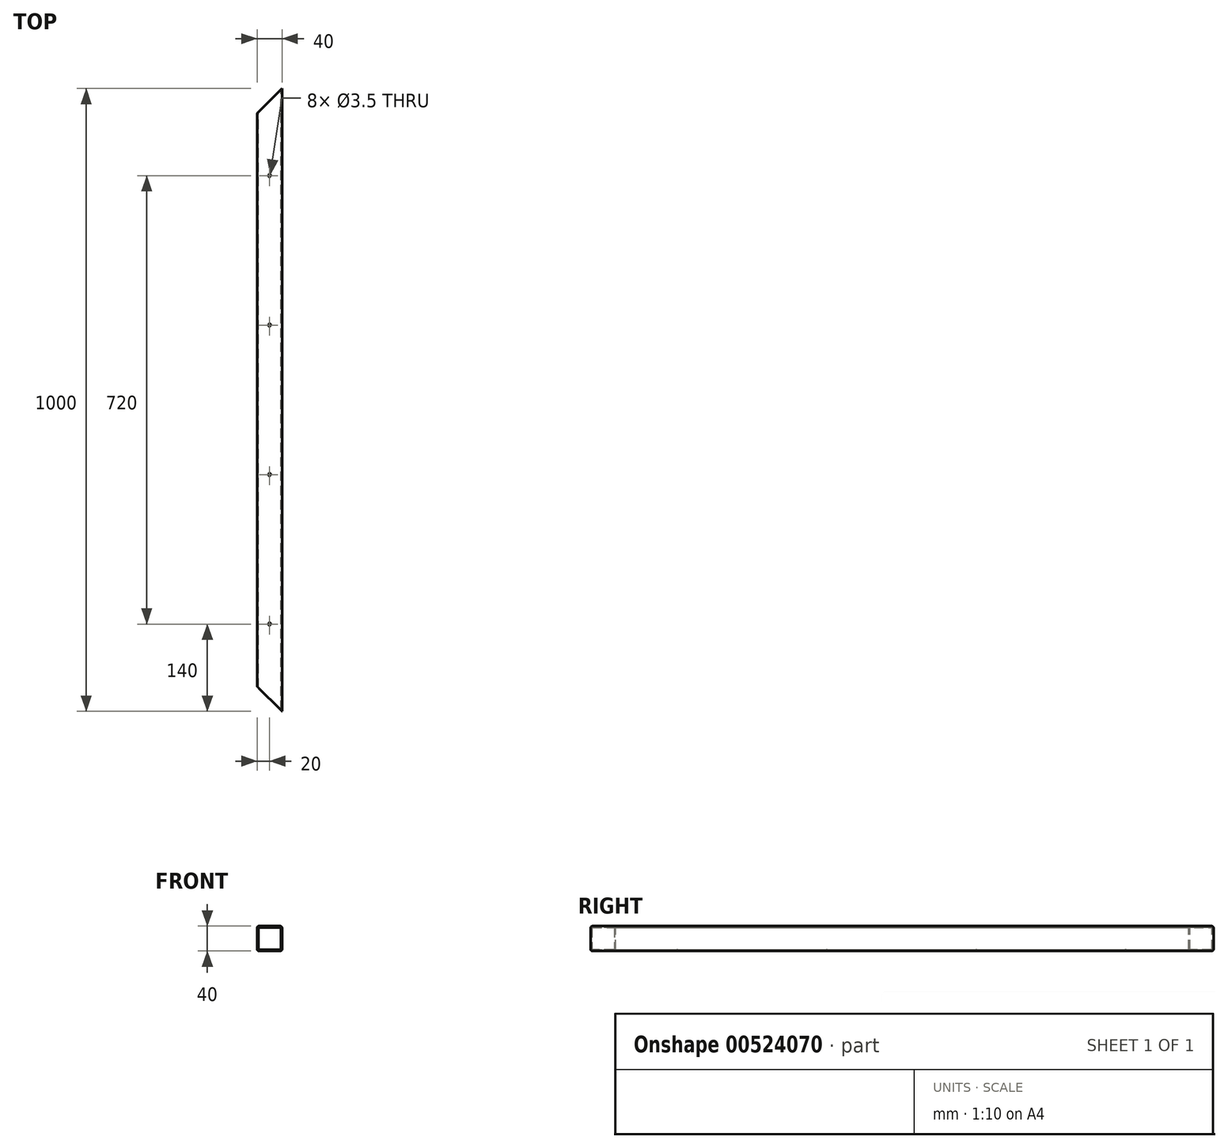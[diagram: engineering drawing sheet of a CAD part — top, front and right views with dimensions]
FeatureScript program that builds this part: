
annotation { "Feature Type Name" : "Feature", "Feature Type Description" : "" }
export const myFeature = defineFeature(function(context is Context, id is Id, definition is map)
    precondition{}
    {
        {
            assignVariable(context, id + "F0", {"name" : "R", "anyValue" : 3});
        }
        {
            assignVariable(context, id + "F1", {"name" : "W", "anyValue" : 2});
        }
        {
            var Q0;
            Q0=qCreatedBy(makeId("Front.planeOp"),FACE);
            var sketch = newSketch(context, id + "F2", { "sketchPlane" : qUnion([Q0])});
            skLineSegment(sketch, "E0.bottom", {"start": v(-20, 20) * mm, "end": v(20, 20) * mm});
            skLineSegment(sketch, "E0.top", {"start": v(-20, -20) * mm, "end": v(20, -20) * mm});
            skLineSegment(sketch, "E0.left", {"start": v(-20, 20) * mm, "end": v(-20, -20) * mm});
            skLineSegment(sketch, "E0.right", {"start": v(20, 20) * mm, "end": v(20, -20) * mm});
            skSolve(sketch);
        }
        {
            var Q0;
            Q0=qSketchRegion(id+"F2",true);
            extrude(context, id + "F3", {"entities" : qUnion([Q0]), "endBound" : BoundingType.SYMMETRIC, "depth" : 1000 * mm, "offsetDistance" : 25 * mm});
        }
        {
            var Q0;
            Q0=makeQuery(id+"F3.opExtrude","SWEPT_EDGE",EDGE,{"disambiguationData":[OSD([sQuery(id+"F2.wireOp",EDGE,"E0.bottom"),sQuery(id+"F2.wireOp",EDGE,"E0.right")])]});
            var Q1;
            Q1=makeQuery(id+"F3.opExtrude","SWEPT_EDGE",EDGE,{"disambiguationData":[OSD([sQuery(id+"F2.wireOp",EDGE,"E0.bottom"),sQuery(id+"F2.wireOp",EDGE,"E0.left")])]});
            var Q2;
            Q2=makeQuery(id+"F3.opExtrude","SWEPT_EDGE",EDGE,{"disambiguationData":[OSD([sQuery(id+"F2.wireOp",EDGE,"E0.top"),sQuery(id+"F2.wireOp",EDGE,"E0.right")])]});
            var Q3;
            Q3=makeQuery(id+"F3.opExtrude","SWEPT_EDGE",EDGE,{"disambiguationData":[OSD([sQuery(id+"F2.wireOp",EDGE,"E0.top"),sQuery(id+"F2.wireOp",EDGE,"E0.left")])]});
            fillet(context, id + "F4", {"entities" : qUnion([Q0, Q1, Q2, Q3]), "radius" : (getVariable(context, 'R')) * mm, "tangentPropagation" : true, "allowEdgeOverflow" : false});
        }
        {
            var Q0;
            Q0=makeQuery(id+"F3.opExtrude","CAP_FACE",FACE,{"disambiguationData":[OSD([sQuery(id+"F2.wireOp",EDGE,"E0.bottom"),sQuery(id+"F2.wireOp",EDGE,"E0.top"),sQuery(id+"F2.wireOp",EDGE,"E0.left"),sQuery(id+"F2.wireOp",EDGE,"E0.right")])],"isStart":false});
            var Q1;
            Q1=makeQuery(id+"F3.opExtrude","CAP_FACE",FACE,{"disambiguationData":[OSD([sQuery(id+"F2.wireOp",EDGE,"E0.bottom"),sQuery(id+"F2.wireOp",EDGE,"E0.top"),sQuery(id+"F2.wireOp",EDGE,"E0.left"),sQuery(id+"F2.wireOp",EDGE,"E0.right")])],"isStart":true});
            shell(context, id + "F5", {"entities" : qUnion([Q0, Q1]), "thickness" : (getVariable(context, 'W')) * mm});
        }
        {
            var Q0;
            Q0=makeQuery(id+"F3.opExtrude","SWEPT_FACE",FACE,{"disambiguationData":[OSD([sQuery(id+"F2.wireOp",EDGE,"E0.bottom")])]});
            var sketch = newSketch(context, id + "F6", { "sketchPlane" : qUnion([Q0])});
            skLineSegment(sketch, "E1.0", {"start": v(-20, -500) * mm, "end": v(-20, 500) * mm, "construction": true});
            skLineSegment(sketch, "E2", {"start": v(-20, 500) * mm, "end": v(20, 500) * mm});
            skLineSegment(sketch, "E3", {"start": v(-20, -460) * mm, "end": v(20, -500) * mm});
            skLineSegment(sketch, "E4", {"start": v(20, -500) * mm, "end": v(-20, -500) * mm});
            skLineSegment(sketch, "E5", {"start": v(-20, -460) * mm, "end": v(-20, -500) * mm});
            skLineSegment(sketch, "E6", {"start": v(20, 500) * mm, "end": v(-20, 460) * mm});
            skLineSegment(sketch, "E7", {"start": v(-20, 460) * mm, "end": v(-20, 500) * mm});
            skSolve(sketch);
        }
        {
            var Q0;
            Q0 = qSketchRegion(id + "F6", true);
            extrude(context, id + "F7", {"entities" : qUnion([Q0]), "operationType" : NewBodyOperationType.REMOVE, "endBound" : BoundingType.THROUGH_ALL, "oppositeDirection" : true, "depth" : 25 * mm, "offsetDistance" : 25 * mm});
        }
        {
            var Q0;
            Q0=makeQuery(id+"F3.opExtrude","SWEPT_FACE",FACE,{"disambiguationData":[OSD([sQuery(id+"F2.wireOp",EDGE,"E0.top")])]});
            var sketch = newSketch(context, id + "F8", { "sketchPlane" : qUnion([Q0])});
            skPoint(sketch, "E8", {"position": v(0, 360) * mm});
            skPoint(sketch, "E9", {"position": v(0, 120) * mm});
            skPoint(sketch, "E10", {"position": v(0, -120) * mm});
            skPoint(sketch, "E11", {"position": v(0, -360) * mm});
            skSolve(sketch);
        }
        {
            var Q0;
            Q0=sQuery(id+"F8.wireOp",VERTEX,"E8");
            var Q1;
            Q1=sQuery(id+"F8.wireOp",VERTEX,"E9");
            var Q2;
            Q2=sQuery(id+"F8.wireOp",VERTEX,"E10");
            var Q3;
            Q3=sQuery(id+"F8.wireOp",VERTEX,"E11");
            var Q4;
            Q4=makeQuery(id+"F3.opExtrude","SWEPT_BODY",BODY,{"disambiguationData":[OSD([sQuery(id+"F2.wireOp",EDGE,"E0.bottom"),sQuery(id+"F2.wireOp",EDGE,"E0.top"),sQuery(id+"F2.wireOp",EDGE,"E0.left"),sQuery(id+"F2.wireOp",EDGE,"E0.right")])]});
            hole(context, id + "F9", {"style" : HoleStyle.C_SINK, "endStyle" : HoleEndStyle.THROUGH, "holeDiameter" : 3.5 * mm, "cSinkDiameter" : 6 * mm, "cSinkAngle" : 90 * degree, "isTappedThrough" : true, "tappedDepth" : 12 * mm, "tapClearance" : 3, "locations" : qUnion([Q0, Q1, Q2, Q3]), "scope" : qUnion([Q4])});
        }
    });
